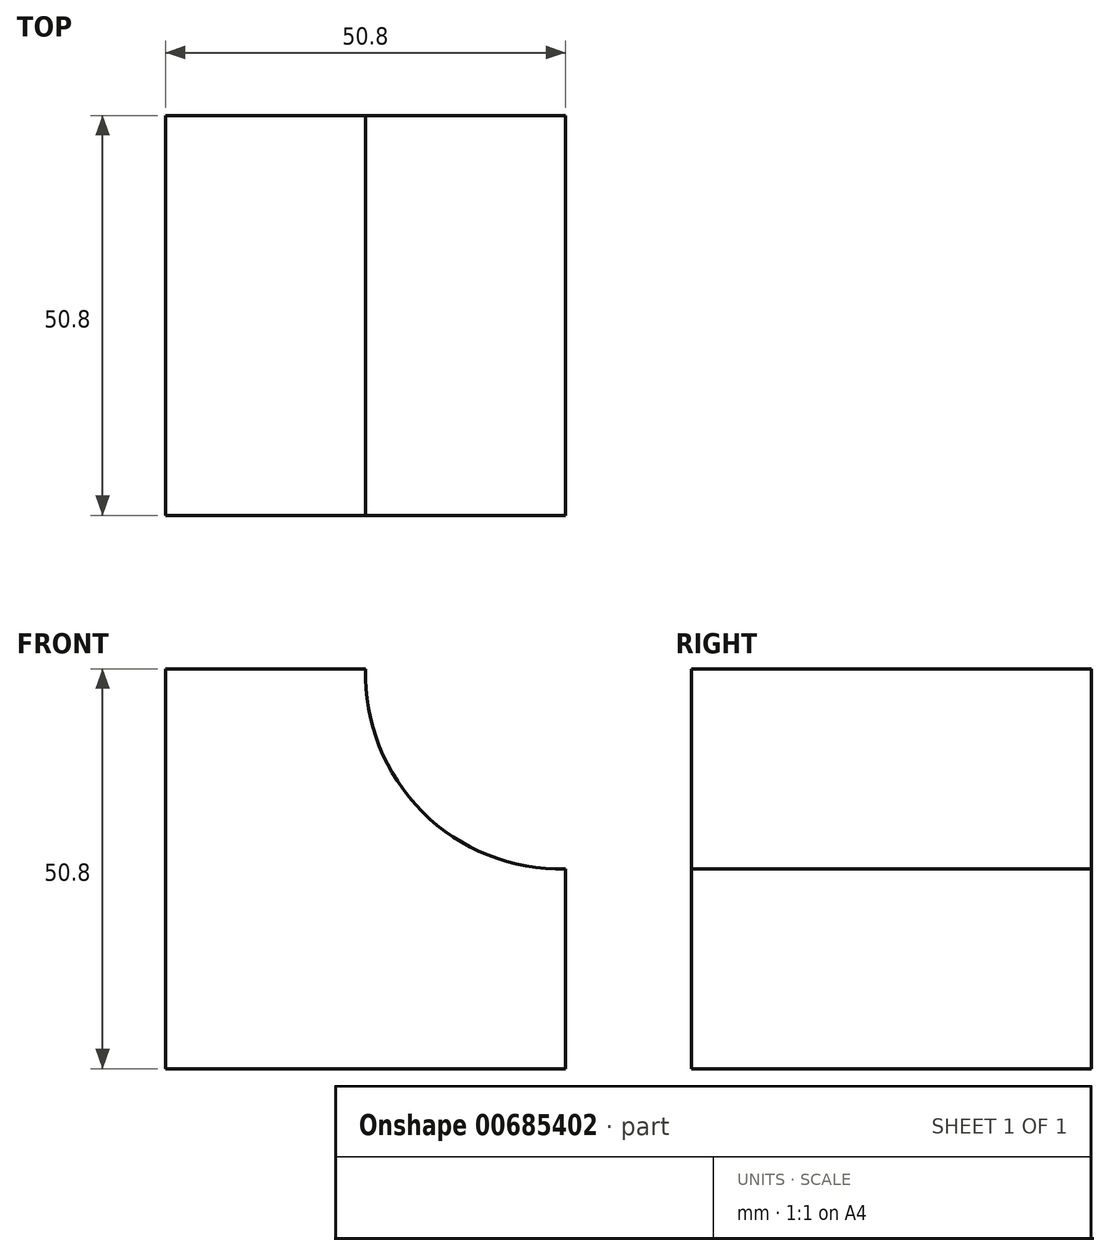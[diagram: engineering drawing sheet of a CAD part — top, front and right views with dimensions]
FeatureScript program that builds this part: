
annotation { "Feature Type Name" : "Feature", "Feature Type Description" : "" }
export const myFeature = defineFeature(function(context is Context, id is Id, definition is map)
    precondition{}
    {
        {
            var Q0;
            Q0=qCreatedBy(makeId("Front.planeOp"),FACE);
            var sketch = newSketch(context, id + "F0", { "sketchPlane" : qUnion([Q0])});
            skLineSegment(sketch, "E0", {"start": v(0, 0) * mm, "end": v(-50.8, 0) * mm});
            skLineSegment(sketch, "E1", {"start": v(-50.8, 0) * mm, "end": v(-50.8, 50.8) * mm});
            skLineSegment(sketch, "E2", {"start": v(-50.8, 50.8) * mm, "end": v(0, 50.8) * mm});
            skLineSegment(sketch, "E3", {"start": v(0, 50.8) * mm, "end": v(0, 0) * mm});
            skSolve(sketch);
        }
        {
            var Q0;
            Q0=makeQuery(id+"F0.imprint","IMPRINT",FACE,{"disambiguationData":[TD([[makeQuery(id+"F0.imprint","IMPRINT",EDGE,{"derivedFrom":sQuery(id+"F0.wireOp",EDGE,"E0")}),-1.0]])]});
            extrude(context, id + "F1", {"entities" : qUnion([Q0]), "depth" : 50.8 * mm, "offsetDistance" : 25.4 * mm});
        }
        {
            var Q0;
            Q0=makeQuery(id+"F1.opExtrude","CAP_FACE",FACE,{"disambiguationData":[OSD([sQuery(id+"F0.wireOp",EDGE,"E0"),sQuery(id+"F0.wireOp",EDGE,"E1"),sQuery(id+"F0.wireOp",EDGE,"E2"),sQuery(id+"F0.wireOp",EDGE,"E3")])],"isStart":false});
            var sketch = newSketch(context, id + "F2", { "sketchPlane" : qUnion([Q0])});
            skArc(sketch, "E4", {"start": v(-25.4, 50.8) * mm, "mid": v(-18.17, 32.63) * mm, "end": v(0, 25.4) * mm});
            skSolve(sketch);
        }
        {
            var Q0;
            {var subQ0=sQuery(id+"F2.wireOp",EDGE,"E4");Q0=makeQuery(id+"F2.imprint","IMPRINT",FACE,{"disambiguationData":[TD([[makeQuery(id+"F2.imprint","IMPRINT",EDGE,{"derivedFrom":subQ0}),1.0]])]});}
            extrude(context, id + "F3", {"entities" : qUnion([Q0]), "operationType" : NewBodyOperationType.REMOVE, "oppositeDirection" : true, "depth" : 50.8 * mm, "offsetDistance" : 25.4 * mm});
        }
    });
